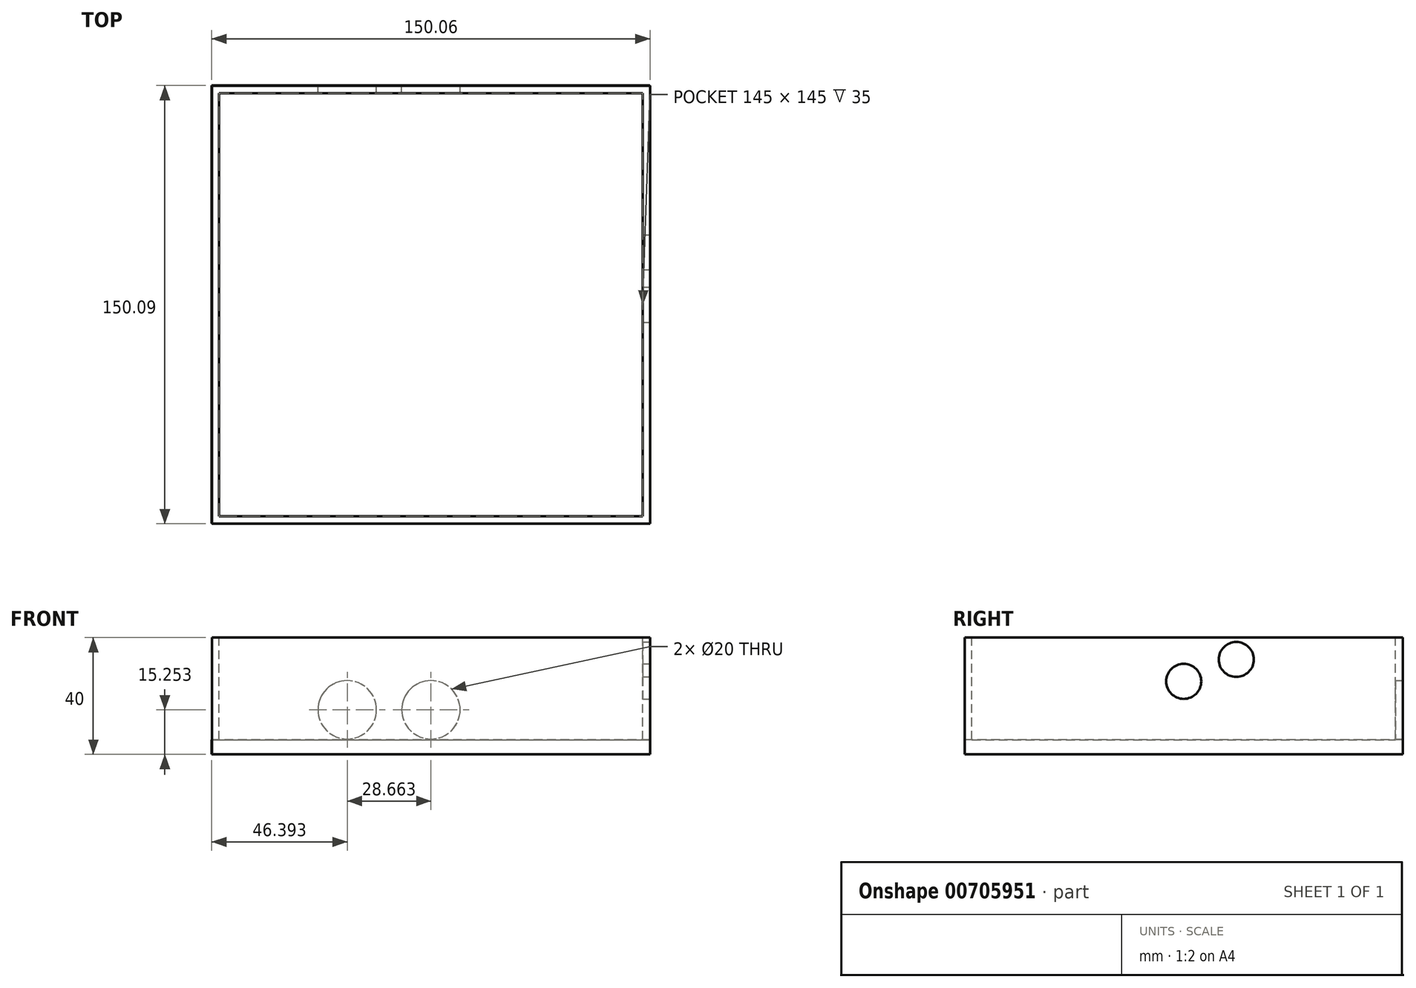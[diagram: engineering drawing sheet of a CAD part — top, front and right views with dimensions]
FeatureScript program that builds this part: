
annotation { "Feature Type Name" : "Feature", "Feature Type Description" : "" }
export const myFeature = defineFeature(function(context is Context, id is Id, definition is map)
    precondition{}
    {
        {
            var Q0;
            Q0=qCreatedBy(makeId("Top.planeOp"),FACE);
            var sketch = newSketch(context, id + "F0", { "sketchPlane" : qUnion([Q0])});
            skLineSegment(sketch, "E0.bottom", {"start": v(-35.97, 116.02) * mm, "end": v(114.03, 116.02) * mm});
            skLineSegment(sketch, "E0.top", {"start": v(-35.97, -33.98) * mm, "end": v(114.03, -33.98) * mm});
            skLineSegment(sketch, "E0.left", {"start": v(-35.97, 116.02) * mm, "end": v(-35.97, -33.98) * mm});
            skLineSegment(sketch, "E0.right", {"start": v(114.03, 116.02) * mm, "end": v(114.03, -33.98) * mm});
            skSolve(sketch);
        }
        {
            var Q0;
            Q0 = qSketchRegion(id + "F0", true);
            extrude(context, id + "F1", {"entities" : qUnion([Q0]), "depth" : 40 * mm, "offsetDistance" : 25 * mm});
        }
        {
            var Q0;
            Q0=makeQuery(id+"F1.opExtrude","CAP_FACE",FACE,{"disambiguationData":[OSD([sQuery(id+"F0.wireOp",EDGE,"E0.bottom"),sQuery(id+"F0.wireOp",EDGE,"E0.top"),sQuery(id+"F0.wireOp",EDGE,"E0.left"),sQuery(id+"F0.wireOp",EDGE,"E0.right")])],"isStart":false});
            var sketch = newSketch(context, id + "F2", { "sketchPlane" : qUnion([Q0])});
            skLineSegment(sketch, "E1.bottom", {"start": v(111.53, 113.52) * mm, "end": v(-33.47, 113.52) * mm});
            skLineSegment(sketch, "E1.top", {"start": v(111.53, -31.48) * mm, "end": v(-33.47, -31.48) * mm});
            skLineSegment(sketch, "E1.left", {"start": v(111.53, 113.52) * mm, "end": v(111.53, -31.48) * mm});
            skLineSegment(sketch, "E1.right", {"start": v(-33.47, 113.52) * mm, "end": v(-33.47, -31.48) * mm});
            skPoint(sketch, "E1.middle", {"position": v(39.03, 41.02) * mm});
            skPoint(sketch, "E1.middle.positionSnap0", {"position": v(-35.97, 41.02) * mm});
            skPoint(sketch, "E1.middle.positionSnap1", {"position": v(39.03, 116.02) * mm});
            skPoint(sketch, "E1.centerSnap0", {"position": v(-35.97, 41.02) * mm});
            skPoint(sketch, "E1.centerSnap1", {"position": v(39.03, 116.02) * mm});
            skSolve(sketch);
        }
        {
            var Q0;
            Q0 = qSketchRegion(id + "F2", true);
            extrude(context, id + "F3", {"entities" : qUnion([Q0]), "operationType" : NewBodyOperationType.REMOVE, "oppositeDirection" : true, "depth" : 135 * mm, "offsetDistance" : 25 * mm});
        }
        {
            var Q0;
            Q0=makeQuery(id+"F1.opExtrude","SWEPT_FACE",FACE,{"disambiguationData":[OSD([sQuery(id+"F0.wireOp",EDGE,"E0.top")])]});
            var sketch = newSketch(context, id + "F4", { "sketchPlane" : qUnion([Q0])});
            skText(sketch, "E2", { "text": "ExPi", "fontName": "AllertaStencil-Regular.ttf"});
            skPoint(sketch, "E3", {"position": v(39.03, 40) * mm});
            const initialGuessF4  = {"E2": [-0.00929, 0.00097, 1, 0, 0.03239]};
            skSetInitialGuess(sketch, initialGuessF4);
            skSolve(sketch);
        }
        {
            var Q0;
            Q0=makeQuery(id+"F1.opExtrude","SWEPT_FACE",FACE,{"disambiguationData":[OSD([sQuery(id+"F0.wireOp",EDGE,"E0.bottom")])]});
            var sketch = newSketch(context, id + "F5", { "sketchPlane" : qUnion([Q0])});
            skPoint(sketch, "E4", {"position": v(-39.03, 15.25) * mm});
            skPoint(sketch, "E4.positionSnap0", {"position": v(-39.03, 0) * mm});
            skPoint(sketch, "E5", {"position": v(-10.36, 15.25) * mm});
            skSolve(sketch);
        }
        {
            var Q0;
            Q0=sQuery(id+"F5.wireOp",VERTEX,"E4");
            var Q1;
            Q1=sQuery(id+"F5.wireOp",VERTEX,"E5");
            var Q2;
            Q2=makeQuery(id+"F1.opExtrude","SWEPT_BODY",BODY,{"disambiguationData":[OSD([sQuery(id+"F0.wireOp",EDGE,"E0.bottom"),sQuery(id+"F0.wireOp",EDGE,"E0.top"),sQuery(id+"F0.wireOp",EDGE,"E0.left"),sQuery(id+"F0.wireOp",EDGE,"E0.right")])]});
            hole(context, id + "F6", {"style" : HoleStyle.SIMPLE, "endStyle" : HoleEndStyle.BLIND, "holeDiameter" : 20 * mm, "majorDiameter" : 5 * mm, "holeDepth" : 5 * mm, "isTappedThrough" : true, "tappedDepth" : 12 * mm, "tapClearance" : 3, "locations" : qUnion([Q0, Q1]), "scope" : qUnion([Q2])});
        }
        {
            var Q0;
            Q0=qCreatedBy(makeId("Top.planeOp"),FACE);
            var sketch = newSketch(context, id + "F7", { "sketchPlane" : qUnion([Q0])});
            skLineSegment(sketch, "E6.bottom", {"start": v(113.97, 116.1) * mm, "end": v(-36.03, 116.1) * mm});
            skLineSegment(sketch, "E6.top", {"start": v(113.97, -33.9) * mm, "end": v(-36.03, -33.9) * mm});
            skLineSegment(sketch, "E6.left", {"start": v(113.97, 116.1) * mm, "end": v(113.97, -33.9) * mm});
            skLineSegment(sketch, "E6.right", {"start": v(-36.03, 116.1) * mm, "end": v(-36.03, -33.9) * mm});
            skPoint(sketch, "E6.middle", {"position": v(38.97, 41.1) * mm});
            skSolve(sketch);
        }
        {
            var Q0;
            Q0 = qSketchRegion(id + "F7", true);
            extrude(context, id + "F8", {"entities" : qUnion([Q0]), "operationType" : NewBodyOperationType.ADD, "depth" : 5 * mm, "offsetDistance" : 25 * mm});
        }
        {
            var Q0;
            Q0=makeQuery(id+"F1.opExtrude","SWEPT_FACE",FACE,{"disambiguationData":[OSD([sQuery(id+"F0.wireOp",EDGE,"E0.right")])]});
            var sketch = newSketch(context, id + "F9", { "sketchPlane" : qUnion([Q0])});
            skPoint(sketch, "E7", {"position": v(41.02, 25) * mm});
            skPoint(sketch, "E7.positionSnap0", {"position": v(41.02, 40) * mm});
            skPoint(sketch, "E8", {"position": v(59.02, 32.5) * mm});
            skSolve(sketch);
        }
        {
            var Q0;
            Q0=sQuery(id+"F9.wireOp",VERTEX,"E8");
            var Q1;
            Q1=sQuery(id+"F9.wireOp",VERTEX,"E7");
            var Q2;
            Q2=makeQuery(id+"F1.opExtrude","SWEPT_BODY",BODY,{"disambiguationData":[OSD([sQuery(id+"F0.wireOp",EDGE,"E0.bottom"),sQuery(id+"F0.wireOp",EDGE,"E0.top"),sQuery(id+"F0.wireOp",EDGE,"E0.left"),sQuery(id+"F0.wireOp",EDGE,"E0.right")])]});
            hole(context, id + "F10", {"style" : HoleStyle.SIMPLE, "endStyle" : HoleEndStyle.BLIND, "holeDiameter" : 12 * mm, "majorDiameter" : 5 * mm, "holeDepth" : 5 * mm, "isTappedThrough" : true, "tappedDepth" : 12 * mm, "tapClearance" : 3, "locations" : qUnion([Q0, Q1]), "scope" : qUnion([Q2])});
        }
    });
